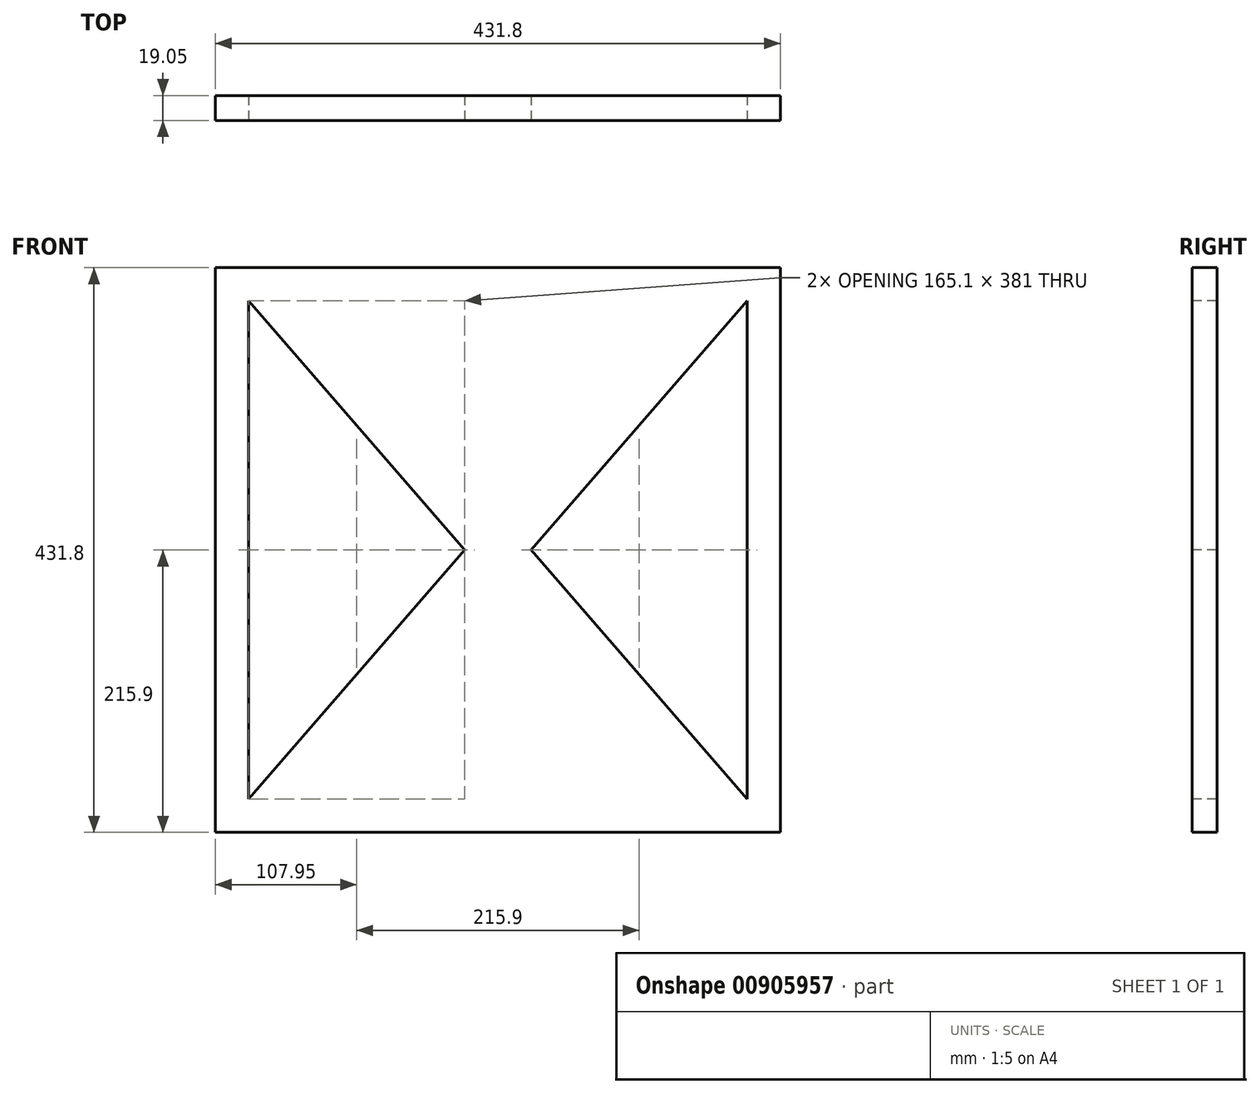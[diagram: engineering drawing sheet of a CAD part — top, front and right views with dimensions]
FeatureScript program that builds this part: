
annotation { "Feature Type Name" : "Feature", "Feature Type Description" : "" }
export const myFeature = defineFeature(function(context is Context, id is Id, definition is map)
    precondition{}
    {
        {
            var Q0;
            Q0=qCreatedBy(makeId("Front.planeOp"),FACE);
            var sketch = newSketch(context, id + "F0", { "sketchPlane" : qUnion([Q0])});
            skLineSegment(sketch, "E0.bottom", {"start": v(0, 0) * mm, "end": v(431.8, 0) * mm});
            skLineSegment(sketch, "E0.top", {"start": v(0, 431.8) * mm, "end": v(431.8, 431.8) * mm});
            skLineSegment(sketch, "E0.left", {"start": v(0, 0) * mm, "end": v(0, 431.8) * mm});
            skLineSegment(sketch, "E0.right", {"start": v(431.8, 0) * mm, "end": v(431.8, 431.8) * mm});
            skSolve(sketch);
        }
        {
            var Q0;
            Q0 = qSketchRegion(id + "F0", true);
            extrude(context, id + "F1", {"entities" : qUnion([Q0]), "depth" : 19.05 * mm, "offsetDistance" : 25.4 * mm});
        }
        {
            var Q0;
            Q0=makeQuery(id+"F1.opExtrude","CAP_FACE",FACE,{"disambiguationData":[OSD([sQuery(id+"F0.wireOp",EDGE,"E0.bottom"),sQuery(id+"F0.wireOp",EDGE,"E0.top"),sQuery(id+"F0.wireOp",EDGE,"E0.left"),sQuery(id+"F0.wireOp",EDGE,"E0.right")])],"isStart":false});
            var sketch = newSketch(context, id + "F2", { "sketchPlane" : qUnion([Q0])});
            skLineSegment(sketch, "E1", {"start": v(25.4, 406.4) * mm, "end": v(25.4, 25.4) * mm});
            skLineSegment(sketch, "E2", {"start": v(25.4, 25.4) * mm, "end": v(190.5, 215.9) * mm});
            skLineSegment(sketch, "E3", {"start": v(190.5, 215.9) * mm, "end": v(25.4, 406.4) * mm});
            skLineSegment(sketch, "E4", {"start": v(241.3, 215.9) * mm, "end": v(406.4, 406.4) * mm});
            skLineSegment(sketch, "E5", {"start": v(406.4, 406.4) * mm, "end": v(406.4, 25.4) * mm});
            skLineSegment(sketch, "E6", {"start": v(406.4, 25.4) * mm, "end": v(241.3, 215.9) * mm});
            skLineSegment(sketch, "E7", {"start": v(190.5, 215.9) * mm, "end": v(241.3, 215.9) * mm, "construction": true});
            skSolve(sketch);
        }
        {
            var Q0;
            Q0 = qSketchRegion(id + "F2", true);
            extrude(context, id + "F3", {"entities" : qUnion([Q0]), "operationType" : NewBodyOperationType.REMOVE, "endBound" : BoundingType.THROUGH_ALL, "oppositeDirection" : true, "depth" : 25.4 * mm, "offsetDistance" : 25.4 * mm});
        }
    });
